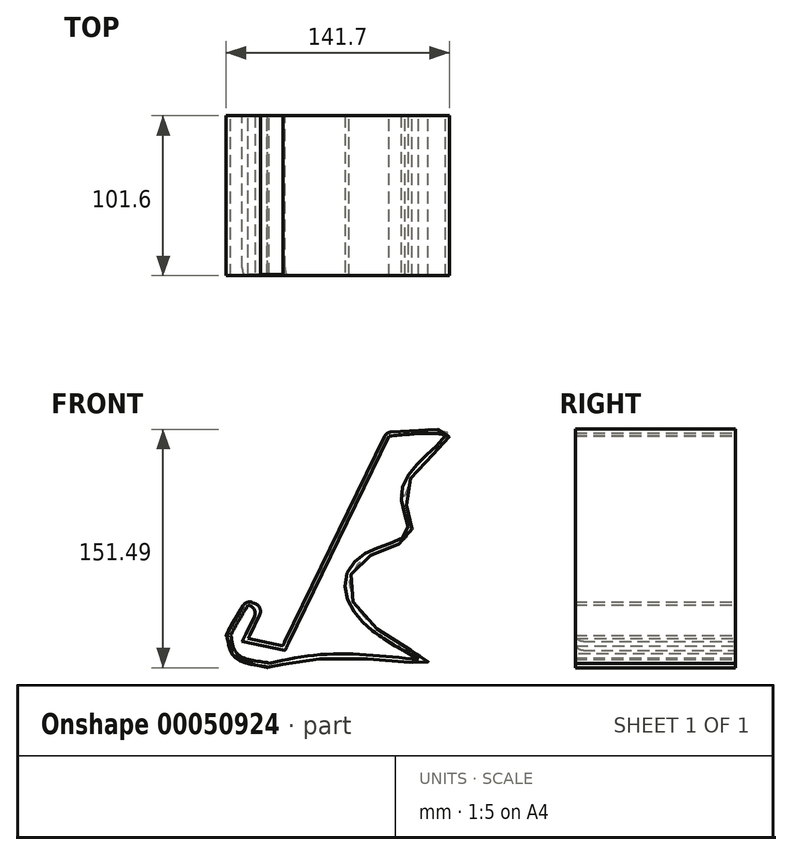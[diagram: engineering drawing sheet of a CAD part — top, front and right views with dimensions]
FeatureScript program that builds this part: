
annotation { "Feature Type Name" : "Feature", "Feature Type Description" : "" }
export const myFeature = defineFeature(function(context is Context, id is Id, definition is map)
    precondition{}
    {
        {
            var Q0;
            Q0=qCreatedBy(makeId("Front.planeOp"),FACE);
            var sketch = newSketch(context, id + "F0", { "sketchPlane" : qUnion([Q0])});
            skLineSegment(sketch, "E0", {"start": v(-22.09, 4.58) * mm, "end": v(0, 0) * mm});
            skLineSegment(sketch, "E1", {"start": v(0, 0) * mm, "end": v(65.9, 135.48) * mm});
            skLineSegment(sketch, "E2", {"start": v(-22.09, 4.58) * mm, "end": v(-12.5, 24.27) * mm});
            skLineSegment(sketch, "E3", {"start": v(-12.5, 24.27) * mm, "end": v(-23, 29.37) * mm});
            skFitSpline(sketch, "E4", {"points": [v(-23, 29.37) * mm, v(-35.96, 6.05) * mm, v(-35.6, 5.79) * mm, v(-30.12, -7.6) * mm, v(-10.04, -13.49) * mm, v(-10.04, -13.85) * mm, v(29.97, -7.79) * mm, v(92.28, -10.15) * mm, v(50.2, 19.24) * mm, v(48.74, 53.13) * mm, v(81.42, 70.56) * mm, v(78.12, 99.35) * mm, v(105.02, 131.45) * mm, v(65.9, 135.48) * mm], "startDerivative": vector(-272.4, -455.16) * mm, "endDerivative": vector(-1001.85, -117.53) * mm});
            skSolve(sketch);
        }
        {
            var Q0;
            Q0 = qSketchRegion(id + "F0", true);
            var Q1;
            Q1=makeQuery(id+"F0.imprint","IMPRINT",FACE,{"disambiguationData":[TD([[makeQuery(id+"F0.imprint","IMPRINT",EDGE,{"derivedFrom":sQuery(id+"F0.wireOp",EDGE,"E0")}),-1.0]])]});
            extrude(context, id + "F1", {"entities" : qUnion([Q0, Q1]), "depth" : 101.6 * mm});
        }
        {
            var Q0;
            Q0=makeQuery(id+"F1.opExtrude","CAP_FACE",FACE,{"disambiguationData":[OSD([sQuery(id+"F0.wireOp",EDGE,"E0"),sQuery(id+"F0.wireOp",EDGE,"E1"),sQuery(id+"F0.wireOp",EDGE,"E2"),sQuery(id+"F0.wireOp",EDGE,"E3"),sQuery(id+"F0.wireOp",EDGE,"E4")])],"isStart":true});
            var Q1;
            Q1=makeQuery(id+"F1.opExtrude","CAP_FACE",FACE,{"disambiguationData":[OSD([sQuery(id+"F0.wireOp",EDGE,"E0"),sQuery(id+"F0.wireOp",EDGE,"E1"),sQuery(id+"F0.wireOp",EDGE,"E2"),sQuery(id+"F0.wireOp",EDGE,"E3"),sQuery(id+"F0.wireOp",EDGE,"E4")])],"isStart":false});
            shell(context, id + "F2", {"entities" : qUnion([Q0, Q1]), "thickness" : 2.54 * mm});
        }
        {
            var Q0;
            {var subQ0=sQuery(id+"F0.wireOp",EDGE,"E0");Q0=makeQuery(id+"F2.opShell","OFFSET_EDGE",EDGE,{"disambiguationData":[OSD([subQ0]),TDD([makeQuery(id+"F1.opExtrude","CAP_EDGE",EDGE,{"disambiguationData":[OSD([subQ0])],"isStart":false})])]});}
            var Q1;
            Q1=makeQuery(id+"F1.opExtrude","SWEPT_EDGE",EDGE,{"disambiguationData":[OSD([sQuery(id+"F0.wireOp",EDGE,"E3"),sQuery(id+"F0.wireOp",EDGE,"E4")])]});
            var Q2;
            Q2=makeQuery(id+"F1.opExtrude","SWEPT_EDGE",EDGE,{"disambiguationData":[OSD([sQuery(id+"F0.wireOp",EDGE,"E2"),sQuery(id+"F0.wireOp",EDGE,"E3")])]});
            var Q3;
            Q3=makeQuery(id+"F2.opShell","OFFSET_EDGE",EDGE,{"disambiguationData":[OSD([sQuery(id+"F0.wireOp",EDGE,"E2"),sQuery(id+"F0.wireOp",EDGE,"E3")])]});
            var Q4;
            Q4=makeQuery(id+"F1.opExtrude","SWEPT_EDGE",EDGE,{"disambiguationData":[OSD([sQuery(id+"F0.wireOp",EDGE,"E1"),sQuery(id+"F0.wireOp",EDGE,"E4")])]});
            fillet(context, id + "F3", {"entities" : qUnion([Q0, Q1, Q2, Q3, Q4]), "radius" : 5.08 * mm, "tangentPropagation" : true, "allowEdgeOverflow" : false});
        }
    });
